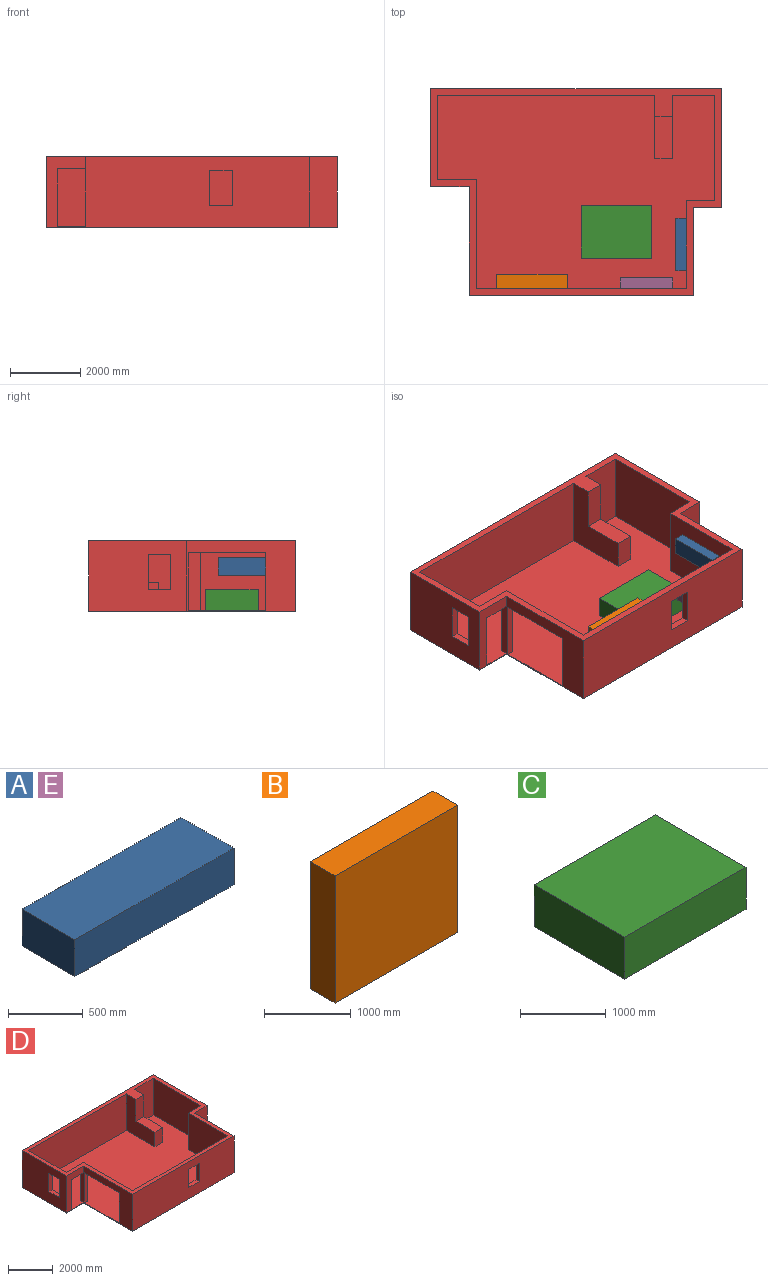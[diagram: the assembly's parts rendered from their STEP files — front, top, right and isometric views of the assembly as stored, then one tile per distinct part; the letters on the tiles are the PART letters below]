
ASSEMBLY  parts=5 mates=7
PART A: 6 faces, bbox 1500x500x300 mm
  f0: plane 1500x300mm, normal (0,1,0), area 450000mm2, adj f1,f3,f4,f5
  f1: plane 500x300mm, normal (-1,0,0), area 150000mm2, adj f0,f2,f4,f5
  f2: plane 1500x300mm, normal (0,-1,0), area 450000mm2, adj f1,f3,f4,f5
  f3: plane 500x300mm, normal (1,0,0), area 150000mm2, adj f0,f2,f4,f5
  f4: plane 1500x500mm, normal (0,0,1), area 750000mm2, adj f0,f1,f2,f3
  f5: plane 1500x500mm, normal (0,0,-1), area 750000mm2, adj f0,f1,f2,f3
PART B: 6 faces, bbox 2000x400x1800 mm
  f0: plane 2000x1800mm, normal (0,1,0), area 3600000mm2, adj f1,f3,f4,f5
  f1: plane 1800x400mm, normal (-1,0,0), area 720000mm2, adj f0,f2,f4,f5
  f2: plane 2000x1800mm, normal (0,-1,0), area 3600000mm2, adj f1,f3,f4,f5
  f3: plane 1800x400mm, normal (1,0,0), area 720000mm2, adj f0,f2,f4,f5
  f4: plane 2000x400mm, normal (0,0,1), area 800000mm2, adj f0,f1,f2,f3
  f5: plane 2000x400mm, normal (0,0,-1), area 800000mm2, adj f0,f1,f2,f3
PART C: 6 faces, bbox 2000x1500x600 mm
  f0: plane 2000x600mm, normal (0,1,0), area 1200000mm2, adj f1,f3,f4,f5
  f1: plane 1500x600mm, normal (-1,0,0), area 900000mm2, adj f0,f2,f4,f5
  f2: plane 2000x600mm, normal (0,-1,0), area 1200000mm2, adj f1,f3,f4,f5
  f3: plane 1500x600mm, normal (1,0,0), area 900000mm2, adj f0,f2,f4,f5
  f4: plane 2000x1500mm, normal (0,0,1), area 3000000mm2, adj f0,f1,f2,f3
  f5: plane 2000x1500mm, normal (0,0,-1), area 3000000mm2, adj f0,f1,f2,f3
PART D: 38 faces, bbox 8300x5900x2025 mm
  f0: plane 6400x2025mm, normal (0,-1,0), area 12310000mm2, adj f8,f10,f20,f22,f34,f35,f36,f37
  f1: plane 6000x2000mm, normal (0,1,0), area 11350000mm2, adj f9,f18,f20,f21,f34,f35,f36,f37
  f2: plane 800x500mm, normal (0,-1,0), area 400000mm2, adj f3,f14,f21,f32
  f3: plane 2000x1800mm, normal (1,0,0), area 2160000mm2, adj f2,f15,f20,f21,f32,f33
  f4: plane 2800x2025mm, normal (-1,0,0), area 5020000mm2, adj f6,f19,f20,f22,f28,f29,f30,f31
  f5: plane 2400x2000mm, normal (1,0,0), area 4150000mm2, adj f7,f13,f20,f21,f28,f29,f30,f31
  f6: plane 2025x1100mm, normal (0,-1,0), area 907500mm2, adj f4,f8,f20,f21,f22,f26,f27
  f7: plane 2000x1100mm, normal (0,1,0), area 880000mm2, adj f5,f8,f9,f20,f21,f26,f27
  f8: plane 3300x2025mm, normal (-1,0,0), area 2977500mm2, adj f0,f6,f7,f20,f21,f22,f23,f24
  f9: plane 3100x2000mm, normal (1,0,0), area 2570000mm2, adj f1,f7,f20,f21,f23,f24,f25
  f10: plane 2500x2025mm, normal (1,0,0), area 5062500mm2, adj f0,f11,f20,f22
  f11: plane 2025x800mm, normal (0,-1,0), area 1620000mm2, adj f10,f12,f20,f22
  f12: plane 3400x2025mm, normal (1,0,0), area 6885000mm2, adj f11,f19,f20,f22
  f13: plane 6200x2000mm, normal (0,-1,0), area 12400000mm2, adj f5,f14,f20,f21
  f14: plane 2000x1800mm, normal (-1,0,0), area 2160000mm2, adj f2,f13,f20,f21,f32,f33
  f15: plane 2000x1200mm, normal (0,-1,0), area 2400000mm2, adj f3,f16,f20,f21
  f16: plane 3000x2000mm, normal (-1,0,0), area 6000000mm2, adj f15,f17,f20,f21
  f17: plane 2000x800mm, normal (0,1,0), area 1600000mm2, adj f16,f18,f20,f21
  f18: plane 2500x2000mm, normal (-1,0,0), area 5000000mm2, adj f1,f17,f20,f21
  f19: plane 8300x2025mm, normal (0,1,0), area 16807500mm2, adj f4,f12,f20,f22
  f20: plane 8300x5900mm, normal (0,0,1), area 5820000mm2, adj f0,f1,f3,f4,f5,f6,f7,f8
  f21: plane 7900x5500mm, normal (0,0,1), area 37740000mm2, adj f1,f2,f3,f5,f6,f7,f8,f9
  f22: plane 8300x5900mm, normal (0,0,-1), area 43560000mm2, adj f0,f4,f6,f8,f10,f11,f12,f19
  f23: plane 2200x200mm, normal (0,0,-1), area 440000mm2, adj f8,f9,f24,f25
  f24: plane 1650x200mm, normal (0,1,0), area 330000mm2, adj f8,f9,f21,f23
  f25: plane 1650x200mm, normal (0,-1,0), area 330000mm2, adj f8,f9,f21,f23
  f26: plane 800x200mm, normal (0,0,-1), area 160000mm2, adj f6,f7,f8,f27
  f27: plane 1650x200mm, normal (1,0,0), area 330000mm2, adj f6,f7,f21,f26
  f28: plane 650x200mm, normal (0,0,-1), area 130000mm2, adj f4,f5,f29,f31
  f29: plane 1000x200mm, normal (0,1,0), area 200000mm2, adj f4,f5,f28,f30
  f30: plane 650x200mm, normal (0,0,1), area 130000mm2, adj f4,f5,f29,f31
  f31: plane 1000x200mm, normal (0,-1,0), area 200000mm2, adj f4,f5,f28,f30
  f32: plane 1200x500mm, normal (0,0,1), area 600000mm2, adj f2,f3,f14,f33
  f33: plane 1200x500mm, normal (0,-1,0), area 600000mm2, adj f3,f14,f20,f32
  f34: plane 650x200mm, normal (0,0,-1), area 130000mm2, adj f0,f1,f35,f37
  f35: plane 1000x200mm, normal (-1,0,0), area 200000mm2, adj f0,f1,f34,f36
  f36: plane 650x200mm, normal (0,0,1), area 130000mm2, adj f0,f1,f35,f37
  f37: plane 1000x200mm, normal (1,0,0), area 200000mm2, adj f0,f1,f34,f36
PART E: same geometry as A
PLACE A rot(axis=(0.58,0.58,0.58),120deg) t=(1600,-3750,-1368.62)mm
PLACE B t=(-3367.04,-4462.67,-2779.17)mm
PLACE C t=(-101.71,-2986.13,-2779.17)mm
PLACE D t=(0,0,-2779.17)mm fixed
PLACE E rot(axis=(1,0,0),90deg) t=(263.29,-4200,-1368.62)mm
MATE planar A.f4 <-> D.f18  axis (1,0,0) through (1900,-3250,-1518.62)mm
MATE planar E.f0 <-> A.f0  axis (0,0,1) through (763.29,-4350,-1268.62)mm
MATE planar B.f2 <-> D.f1  axis (0,-1,0) through (-2505.92,-4500,-1879.17)mm
MATE planar B.f5 <-> D.f21  axis (0,0,-1) through (-2505.92,-4300,-2779.17)mm
MATE parallel E.f0 <-> A.f0  axis (0,0,1) through (763.29,-4350,-1268.62)mm
MATE planar E.f4 <-> D.f1  axis (0,-1,0) through (763.29,-4500,-1518.62)mm
MATE planar C.f5 <-> D.f21  axis (0,0,-1) through (-101.71,-2886.13,-2779.17)mm
